# Revit family: IS_CerafineModelO_BC554_BIM_GB
name_source: partatom
category: Plumbing Fixtures
units: mm (PartAtom-declared; Revit-internal decimal feet)

## family parameters
Always vertical = No
Cut with Voids When Loaded = No
OmniClass Number = 23.45.55.17
OmniClass Title = Mixing Faucets
Part Type = Normal
Room Calculation Point = No
Round Connector Dimension = Use Diameter
Shared = No
Work Plane-Based = No

## types (2) — shared parameters
Accessories = https://www.idealspec.co.uk
AreaUnits = millimeters
AssetType = Fixed
BIMObjectName = ISI_IdealStandard_Water supply fittings for wash basins and troughs_CerafineO_BC554
BIMobject category = Taps & Mixers
BIMobject category code = sanitary-taps-mixers
BIMobject main category = Sanitary
BIMobject main category code = sanitary
Brand = Ideal Standard
Brand url = http://www.idealstandard.co.uk
ConnectionType = Plumbing
CurrencyUnit = £
CurrentRevision = 1
Date of publishing = 09/09/2020
DurationUnit = Year
Edition number = 1
ExpectedLife = 30
FaucetFunction = MIXED
FaucetOperation = OTHER
FaucetType = OTHER
Help = https://www.idealspec.co.uk
IFC Classification = Sanitary Terminal
IfcExportAs = IfcValveType
IfcExportType = FAUCET
Installation instructions = https://www.idealspec.co.uk
InstallationInstructions = https://www.idealspec.co.uk
IsHighPressure = No
LinearUnits = millimeters
MainColor = Chrome
MaintenanceInformation = https://www.idealspec.co.uk
Manufacturer = Ideal Standard
Manufacturer name = Ideal Standard
ManufacturerURL = https://www.idealspec.co.uk
Material = Brass
Material main = Brass
ModelNumber = BC554AA
ModelReference = CERAFINE O Single metal lever basin mixer DN 15 with 126 mm spout projection with read / blue marking, 120 Height. Flexible connection hoses. Chrome finish.
NBS Reference Code = 45-35-70/371
NBS Reference Description = Water supply fittings for wash basins and troughs
Name = Water supply fittings for wash basins and troughs_CerafineO_BC554_IdealStandard
NettWeight = 1,23 KG
NominalDepth = 166 mm
NominalHeight = 176 mm
NominalLength = 166 mm
NominalWidth = 50 mm
OmniClass Code = 23.45.55.17
OmniClass Description = Mixing Faucets
Product Guid = 39096454-8d2d-424a-9d95-5feb3a3d50dc
Product SKU = BC554
Product certification = https://www.idealspec.co.uk
Product data url = https://bimobject.com
Product family = CERAFINE MODEL O
Product group = BASIN MIXER
Product name = A_CERAFINE O BSN MXR H120 RMTD NO PUW
Product url = https://www.idealspec.co.uk
ProductInformation = https://www.idealspec.co.uk
QR code = http://bimobject.com
Shape = Sculptured
Size = 50 x 166 x 176 mm
Space = Internal
SpareParts = https://fastpart-spares.co.uk
Technical description = https://www.idealspec.co.uk
TestPressure = 10 bar
UNSPSC Code = 30181700
URL = https://www.idealspec.co.uk
Uniclass 1.4 Code = L725111
Uniclass 1.4 Description = Mixer taps
Uniclass 2.0 Code = Pr_40_30_96_95
Uniclass 2.0 Description = Washbasin Manual Valves
Uniclass 2015 Code = Pr_40_20_87_98
Uniclass 2015 Name = Washbasin taps
Uniclass2015Code = Pr_40_20_87_98
Uniclass2015Title = Washbasin taps
Uniclass2015Version = v1.20
ValveMechanism = Thermostatic
ValveOperation = Lever
Version = 1
VolumeUnits = Litres
WRASURL = https://www.wras.co.uk
WarrantyDescription = Manufacturers Warranty
WarrantyDurationParts = 5
WarrantyDurationUnit = Year
WarrantyGuarantorParts = https://www.idealspec.co.uk
zero-valued in all types: MaterialThickness

## per-type parameters (varying)
| type | BarCode | Color | Description | Features | Finish | GTIN code | Model |
| BC554AA - CERAFINE O BASIN MIXER H120 RIM-MOUNTED 5L PER MINUTE - CHROME | 3800861074991 | Chrome | CERAFINE O Single metal lever basin mixer DN 15 with 126 mm spout projection with read / blue marking, 120 Height Flexible connection hoses  - Chrome | Single metal lever shower mixer AP DN 15 with backflow preventer S-connections concealed and noise-suppressed, 50-55 mm Available in or matt  - Chrome | Chrome | https://3800861074991 | BC554AA |
| BC554XG - CERAFINE O BASIN MIXER H120 RIM-MOUNTED 5L PER MINUTE - SILK BLACK | 3800861101307 | Silk Black | CERAFINE O Single metal lever basin mixer DN 15 with 126 mm spout projection with read / blue marking, 120 Height Flexible connection hoses  - Silk Black | Single metal lever shower mixer AP DN 15 with backflow preventer S-connections concealed and noise-suppressed, 50-55 mm Available in or matt  - Black & Chrome | Silk Black | https://3800861101307 | BC554XG |

## geometry (parser evidence)
native form markers: Sweep x2
no freeform markers — native parametric forms only
